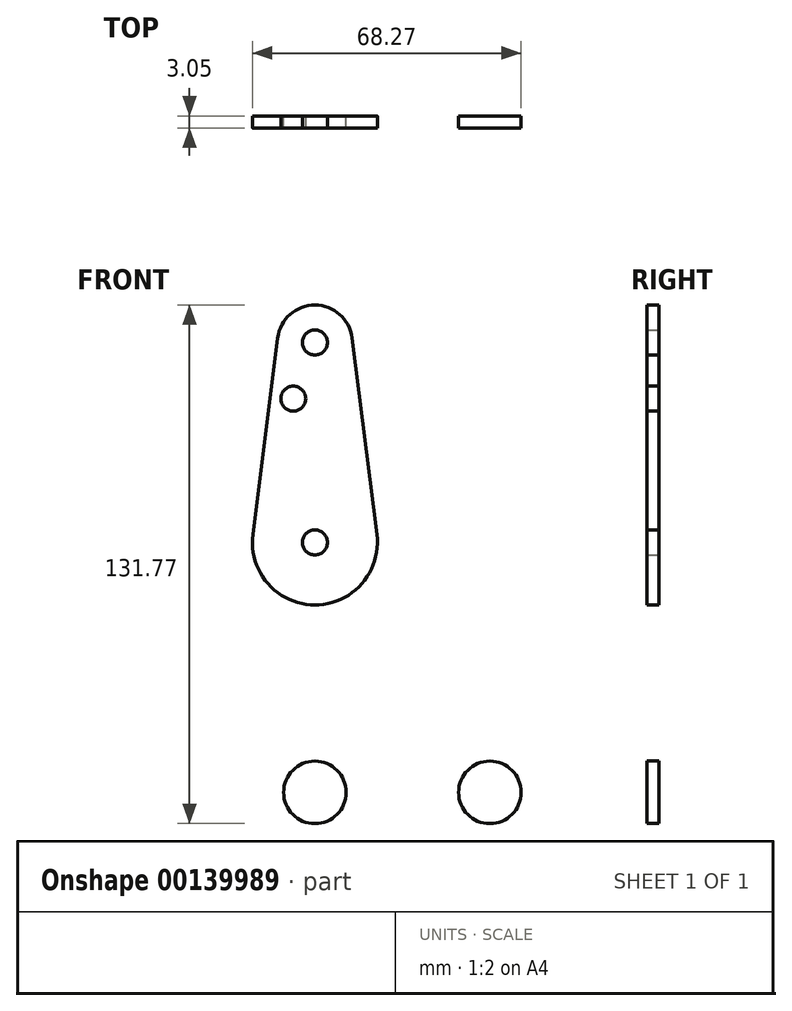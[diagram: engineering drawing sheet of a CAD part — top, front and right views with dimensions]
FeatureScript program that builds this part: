
annotation { "Feature Type Name" : "Feature", "Feature Type Description" : "" }
export const myFeature = defineFeature(function(context is Context, id is Id, definition is map)
    precondition{}
    {
        {
            var Q0;
            Q0=qCreatedBy(makeId("Front.planeOp"),FACE);
            var sketch = newSketch(context, id + "F0", { "sketchPlane" : qUnion([Q0])});
            skCircle(sketch, "E0", {"center": v(0, 0) * mm, "radius": 7.94 * mm});
            skLineSegment(sketch, "E1", {"start": v(0, 0) * mm, "end": v(44.45, 0) * mm, "construction": true});
            skLineSegment(sketch, "E2", {"start": v(0, 0) * mm, "end": v(0, 114.3) * mm, "construction": true});
            skCircle(sketch, "E3", {"center": v(0, 114.3) * mm, "radius": 9.53 * mm});
            skCircle(sketch, "E4", {"center": v(0, 63.5) * mm, "radius": 15.88 * mm});
            skCircle(sketch, "E5", {"center": v(44.45, 0) * mm, "radius": 7.94 * mm});
            skLineSegment(sketch, "E6", {"start": v(15.75, 65.48) * mm, "end": v(9.45, 115.5) * mm});
            skLineSegment(sketch, "E7", {"start": v(-15.75, 65.48) * mm, "end": v(-9.45, 115.5) * mm});
            skLineSegment(sketch, "E8", {"start": v(15.75, 61.52) * mm, "end": v(9.94, 15.44) * mm});
            skLineSegment(sketch, "E9", {"start": v(18.27, 6.5) * mm, "end": v(44.01, 7.93) * mm});
            skLineSegment(sketch, "E10", {"start": v(0, -7.94) * mm, "end": v(44.45, -7.94) * mm});
            skCircle(sketch, "E11", {"center": v(0, 114.3) * mm, "radius": 3.18 * mm});
            skCircle(sketch, "E12", {"center": v(0, 63.5) * mm, "radius": 3.18 * mm});
            skCircle(sketch, "E13", {"center": v(0, 0) * mm, "radius": 3.18 * mm});
            skCircle(sketch, "E14", {"center": v(44.45, 0) * mm, "radius": 3.18 * mm});
            skCircle(sketch, "E15", {"center": v(-5.5, 100.03) * mm, "radius": 3.18 * mm});
            skArc(sketch, "E16.filletArc", {"start": v(9.94, 15.44) * mm, "mid": v(12.02, 9.02) * mm, "end": v(18.27, 6.5) * mm});
            skLineSegment(sketch, "E17", {"start": v(-7.94, 0) * mm, "end": v(-15.75, 61.52) * mm});
            skSolve(sketch);
        }
        {
            var Q0;
            Q0 = qSketchRegion(id + "F0", true);
            extrude(context, id + "F1", {"entities" : qUnion([Q0]), "depth" : 3.05 * mm});
        }
    });
